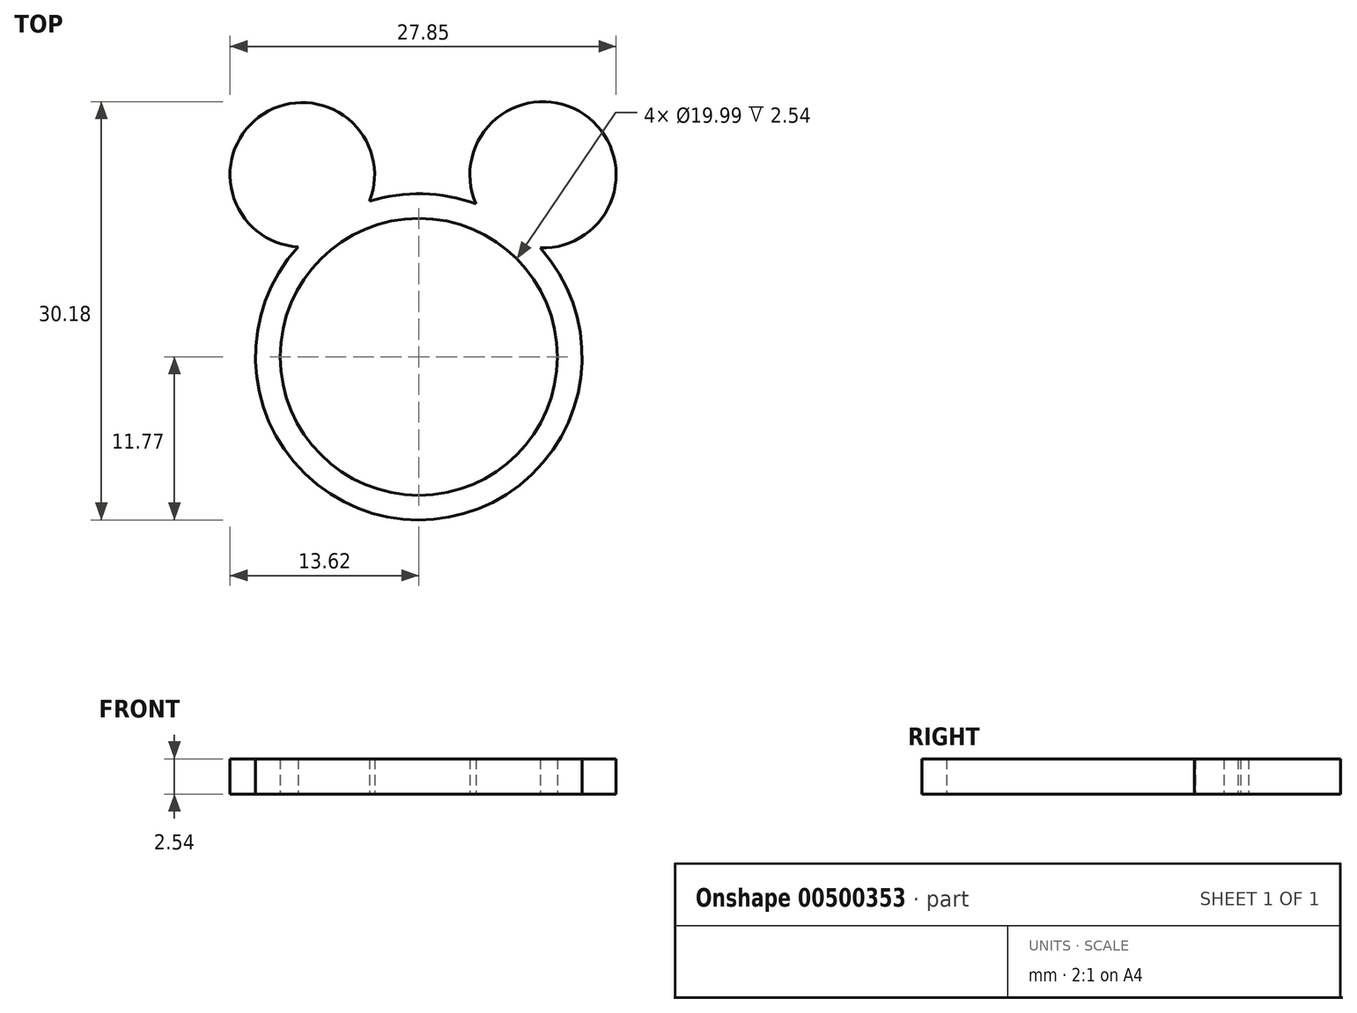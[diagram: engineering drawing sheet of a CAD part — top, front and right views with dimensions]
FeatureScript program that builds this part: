
annotation { "Feature Type Name" : "Feature", "Feature Type Description" : "" }
export const myFeature = defineFeature(function(context is Context, id is Id, definition is map)
    precondition{}
    {
        {
            var Q0;
            Q0=qCreatedBy(makeId("Top.planeOp"),FACE);
            var sketch = newSketch(context, id + "F0", { "sketchPlane" : qUnion([Q0])});
            skCircle(sketch, "E0", {"center": v(0, 0) * mm, "radius": 10 * mm});
            skArc(sketch, "E1", {"start": v(-8.7, 7.93) * mm, "mid": v(-0.04, -11.77) * mm, "end": v(8.76, 7.87) * mm});
            skArc(sketch, "E2", {"start": v(-3.56, 11.22) * mm, "mid": v(-11.21, 17.53) * mm, "end": v(-8.7, 7.93) * mm});
            skArc(sketch, "E3", {"start": v(8.76, 7.87) * mm, "mid": v(11.93, 17.5) * mm, "end": v(4.12, 11.03) * mm});
            skPoint(sketch, "E4.orphan", {"position": v(0, 18.51) * mm});
            skPoint(sketch, "E5.orphan", {"position": v(-16.81, 7.76) * mm});
            skPoint(sketch, "E6.orphan", {"position": v(17.91, 7.76) * mm});
            skArc(sketch, "E7.trimOffspring", {"start": v(4.12, 11.03) * mm, "mid": v(0.3, 11.77) * mm, "end": v(-3.56, 11.22) * mm});
            skSolve(sketch);
        }
        {
            var Q0;
            Q0 = qSketchRegion(id + "F0", true);
            extrude(context, id + "F1", {"entities" : qUnion([Q0]), "depth" : 2.54 * mm, "offsetDistance" : 25.4 * mm});
        }
    });
